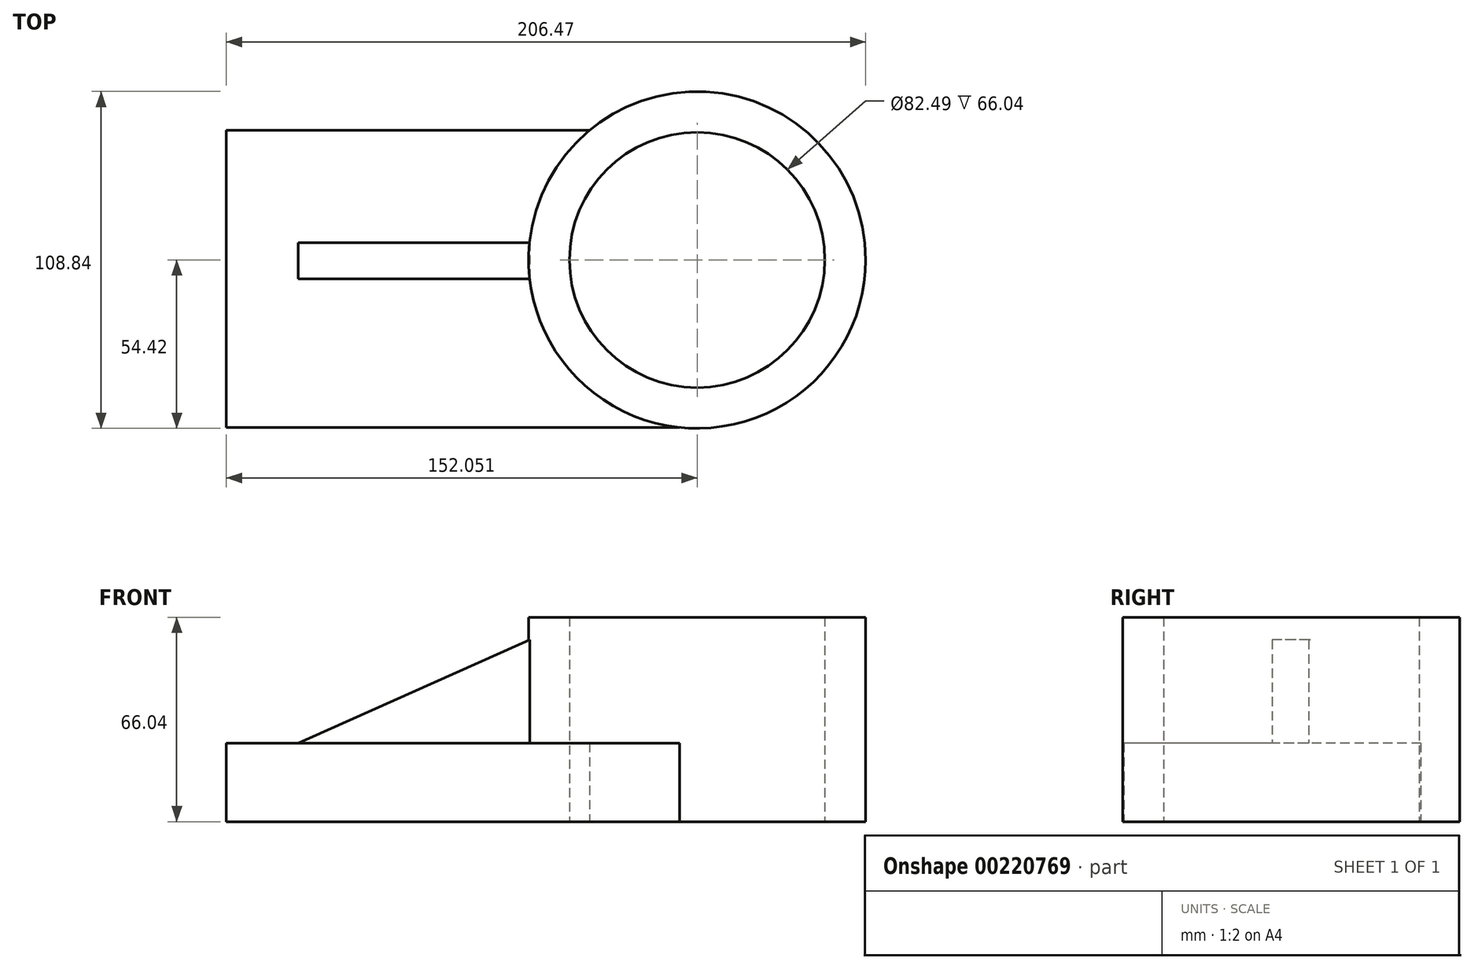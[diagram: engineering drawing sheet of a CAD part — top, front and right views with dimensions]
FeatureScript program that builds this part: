
annotation { "Feature Type Name" : "Feature", "Feature Type Description" : "" }
export const myFeature = defineFeature(function(context is Context, id is Id, definition is map)
    precondition{}
    {
        {
            var Q0;
            Q0=qCreatedBy(makeId("Top.planeOp"),FACE);
            var sketch = newSketch(context, id + "F0", { "sketchPlane" : qUnion([Q0])});
            skCircle(sketch, "E0", {"center": v(75.93, 0) * mm, "radius": 54.42 * mm});
            skCircle(sketch, "E1", {"center": v(75.93, 0) * mm, "radius": 41.25 * mm});
            skSolve(sketch);
        }
        {
            var Q0;
            Q0=makeQuery(id+"F0.imprint","IMPRINT",FACE,{"disambiguationData":[TD([[makeQuery(id+"F0.imprint","IMPRINT",EDGE,{"derivedFrom":sQuery(id+"F0.wireOp",EDGE,"E0")}),1.0]])]});
            extrude(context, id + "F1", {"entities" : qUnion([Q0]), "depth" : 66.04 * mm});
        }
        {
            var Q0;
            Q0=qCreatedBy(makeId("Top.planeOp"),FACE);
            var sketch = newSketch(context, id + "F2", { "sketchPlane" : qUnion([Q0])});
            skLineSegment(sketch, "E2.bottom", {"start": v(75.54, 41.83) * mm, "end": v(-76.12, 41.83) * mm});
            skLineSegment(sketch, "E2.top", {"start": v(75.54, -54.13) * mm, "end": v(-76.12, -54.13) * mm});
            skLineSegment(sketch, "E2.left", {"start": v(75.54, 41.83) * mm, "end": v(75.54, -54.13) * mm});
            skLineSegment(sketch, "E2.right", {"start": v(-76.12, 41.83) * mm, "end": v(-76.12, -54.13) * mm});
            skSolve(sketch);
        }
        {
            var Q0;
            Q0=makeQuery(id+"F2.imprint","IMPRINT",FACE,{"disambiguationData":[TD([[makeQuery(id+"F2.imprint","IMPRINT",EDGE,{"derivedFrom":sQuery(id+"F2.wireOp",EDGE,"E2.bottom")}),1.0]])]});
            extrude(context, id + "F3", {"entities" : qUnion([Q0]), "operationType" : NewBodyOperationType.ADD, "depth" : 25.4 * mm});
        }
        {
            var Q0;
            {var subQ0=sQuery(id+"F2.wireOp",EDGE,"E2.left");Q0=makeQuery(id+"F3.boolean.opBoolean","SPLIT",FACE,{"disambiguationData":[TD([makeQuery(id+"F1.opExtrude","SWEPT_FACE",FACE,{"disambiguationData":[OSD([sQuery(id+"F0.wireOp",EDGE,"E1")])]})])],"derivedFrom":makeQuery(id+"F3.opExtrude","CAP_FACE",FACE,{"disambiguationData":[OSD([sQuery(id+"F2.wireOp",EDGE,"E2.bottom"),sQuery(id+"F2.wireOp",EDGE,"E2.top"),subQ0,sQuery(id+"F2.wireOp",EDGE,"E2.right")])],"isStart":false})});}
            var Q1;
            Q1=sQuery(id+"F0.wireOp",EDGE,"E1");
            extrude(context, id + "F4", {"entities" : qUnion([Q0]), "operationType" : NewBodyOperationType.REMOVE, "surfaceEntities" : qUnion([Q1]), "oppositeDirection" : true, "depth" : 50.8 * mm});
        }
        {
            var Q0;
            Q0=makeQuery(id+"F3.opExtrude","SWEPT_FACE",FACE,{"disambiguationData":[OSD([sQuery(id+"F2.wireOp",EDGE,"E2.right")])]});
            var sketch = newSketch(context, id + "F5", { "sketchPlane" : qUnion([Q0])});
            skLineSegment(sketch, "E3", {"start": v(-54.42, 0) * mm, "end": v(-54.42, 66.04) * mm});
            skLineSegment(sketch, "E4", {"start": v(54.42, 66.04) * mm, "end": v(54.42, 0) * mm});
            skLineSegment(sketch, "E5.bottom", {"start": v(6.15, 25.4) * mm, "end": v(-5.55, 25.4) * mm});
            skLineSegment(sketch, "E5.top", {"start": v(6.15, 58.7) * mm, "end": v(-5.55, 58.7) * mm});
            skLineSegment(sketch, "E5.left", {"start": v(6.15, 25.4) * mm, "end": v(6.15, 58.7) * mm});
            skLineSegment(sketch, "E5.right", {"start": v(-5.55, 25.4) * mm, "end": v(-5.55, 58.7) * mm});
            skSolve(sketch);
        }
        {
            var Q0;
            Q0 = qSketchRegion(id + "F5", true);
            extrude(context, id + "F6", {"entities" : qUnion([Q0]), "operationType" : NewBodyOperationType.ADD, "oppositeDirection" : true, "depth" : 101.6 * mm});
        }
        {
            var Q0;
            Q0=makeQuery(id+"F6.opExtrude","SWEPT_FACE",FACE,{"disambiguationData":[OSD([sQuery(id+"F5.wireOp",EDGE,"E5.left")])]});
            var sketch = newSketch(context, id + "F7", { "sketchPlane" : qUnion([Q0])});
            skLineSegment(sketch, "E6", {"start": v(-52.88, 25.4) * mm, "end": v(-76.12, 25.4) * mm});
            skLineSegment(sketch, "E7", {"start": v(-76.12, 25.4) * mm, "end": v(-76.12, 58.7) * mm});
            skLineSegment(sketch, "E8", {"start": v(-76.12, 58.7) * mm, "end": v(21.86, 58.7) * mm});
            skLineSegment(sketch, "E9", {"start": v(21.86, 58.7) * mm, "end": v(-52.88, 25.4) * mm});
            skSolve(sketch);
        }
        {
            var Q0;
            Q0=makeQuery(id+"F7.imprint","IMPRINT",FACE,{"disambiguationData":[TD([[makeQuery(id+"F7.imprint","IMPRINT",EDGE,{"derivedFrom":sQuery(id+"F7.wireOp",EDGE,"E6")}),-1.0]])]});
            extrude(context, id + "F8", {"entities" : qUnion([Q0]), "operationType" : NewBodyOperationType.REMOVE, "oppositeDirection" : true, "depth" : 25.4 * mm});
        }
    });
